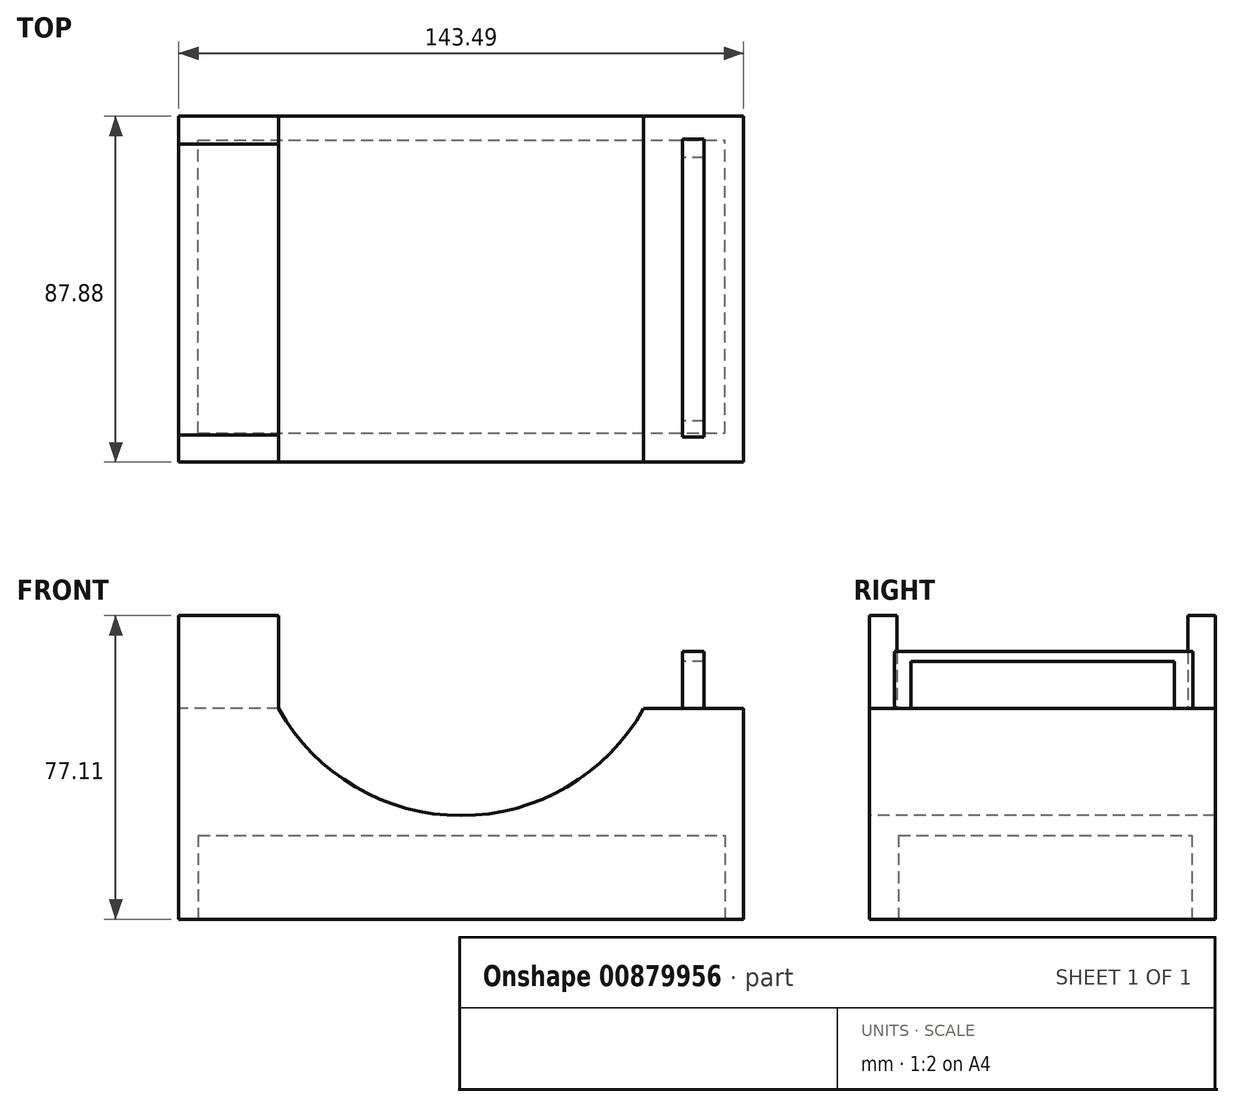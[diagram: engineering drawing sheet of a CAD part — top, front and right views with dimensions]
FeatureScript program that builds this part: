
annotation { "Feature Type Name" : "Feature", "Feature Type Description" : "" }
export const myFeature = defineFeature(function(context is Context, id is Id, definition is map)
    precondition{}
    {
        {
            var Q0;
            Q0=qCreatedBy(makeId("Front.planeOp"),FACE);
            var sketch = newSketch(context, id + "F0", { "sketchPlane" : qUnion([Q0])});
            skLineSegment(sketch, "E0.bottom", {"start": v(-31.97, 19.52) * mm, "end": v(60.72, 19.52) * mm});
            skLineSegment(sketch, "E0.top", {"start": v(-31.97, -33.97) * mm, "end": v(60.72, -33.97) * mm});
            skLineSegment(sketch, "E0.left", {"start": v(-31.97, 19.52) * mm, "end": v(-31.97, -33.97) * mm});
            skLineSegment(sketch, "E0.right", {"start": v(60.72, 19.52) * mm, "end": v(60.72, -33.97) * mm});
            skSolve(sketch);
        }
        {
            var Q0;
            Q0=makeQuery(id+"F0.imprint","IMPRINT",FACE,{"disambiguationData":[TD([[makeQuery(id+"F0.imprint","IMPRINT",EDGE,{"derivedFrom":sQuery(id+"F0.wireOp",EDGE,"E0.bottom")}),-1.0]])]});
            extrude(context, id + "F1", {"entities" : qUnion([Q0]), "depth" : 87.88 * mm, "offsetDistance" : 25.4 * mm});
        }
        {
            var Q0;
            Q0=makeQuery(id+"F1.opExtrude","CAP_FACE",FACE,{"disambiguationData":[OSD([sQuery(id+"F0.wireOp",EDGE,"E0.bottom"),sQuery(id+"F0.wireOp",EDGE,"E0.top"),sQuery(id+"F0.wireOp",EDGE,"E0.left"),sQuery(id+"F0.wireOp",EDGE,"E0.right")])],"isStart":false});
            var sketch = newSketch(context, id + "F2", { "sketchPlane" : qUnion([Q0])});
            skArc(sketch, "E1", {"start": v(-31.97, 19.52) * mm, "mid": v(14.38, -7.65) * mm, "end": v(60.72, 19.52) * mm});
            skSolve(sketch);
        }
        {
            var Q0;
            Q0=makeQuery(id+"F2.imprint","IMPRINT",FACE,{"disambiguationData":[TD([[makeQuery(id+"F2.imprint","IMPRINT",EDGE,{"derivedFrom":sQuery(id+"F2.wireOp",EDGE,"E1")}),1.0]])]});
            extrude(context, id + "F3", {"entities" : qUnion([Q0]), "operationType" : NewBodyOperationType.REMOVE, "oppositeDirection" : true, "depth" : 162.8 * mm, "offsetDistance" : 25.4 * mm});
        }
        {
            var Q0;
            Q0=makeQuery(id+"F1.opExtrude","SWEPT_FACE",FACE,{"disambiguationData":[OSD([sQuery(id+"F0.wireOp",EDGE,"E0.right")])]});
            extrude(context, id + "F4", {"entities" : qUnion([Q0]), "operationType" : NewBodyOperationType.ADD, "depth" : 25.4 * mm, "offsetDistance" : 25.4 * mm});
        }
        {
            var Q0;
            Q0=makeQuery(id+"F1.opExtrude","SWEPT_FACE",FACE,{"disambiguationData":[OSD([sQuery(id+"F0.wireOp",EDGE,"E0.left")])]});
            extrude(context, id + "F5", {"entities" : qUnion([Q0]), "operationType" : NewBodyOperationType.ADD, "depth" : 25.4 * mm, "offsetDistance" : 25.4 * mm});
        }
        {
            var Q0;
            Q0=makeQuery(id+"F4.opExtrude","SWEPT_FACE",FACE,{"disambiguationData":[OSD([sQuery(id+"F0.wireOp",EDGE,"E0.bottom"),sQuery(id+"F0.wireOp",EDGE,"E0.right"),sQuery(id+"F2.wireOp",EDGE,"E1")])]});
            var sketch = newSketch(context, id + "F6", { "sketchPlane" : qUnion([Q0])});
            skLineSegment(sketch, "E2.bottom", {"start": v(70.54, -81.5) * mm, "end": v(76.1, -81.5) * mm});
            skLineSegment(sketch, "E2.top", {"start": v(70.54, -5.79) * mm, "end": v(76.1, -5.79) * mm});
            skLineSegment(sketch, "E2.left", {"start": v(70.54, -81.5) * mm, "end": v(70.54, -5.79) * mm});
            skLineSegment(sketch, "E2.right", {"start": v(76.1, -81.5) * mm, "end": v(76.1, -5.79) * mm});
            skSolve(sketch);
        }
        {
            var Q0;
            Q0 = qSketchRegion(id + "F6", true);
            extrude(context, id + "F7", {"entities" : qUnion([Q0]), "operationType" : NewBodyOperationType.ADD, "depth" : 14.48 * mm, "offsetDistance" : 25.4 * mm});
        }
        {
            var Q0;
            Q0=makeQuery(id+"F7.opExtrude","SWEPT_FACE",FACE,{"disambiguationData":[OSD([sQuery(id+"F6.wireOp",EDGE,"E2.left")])]});
            var sketch = newSketch(context, id + "F8", { "sketchPlane" : qUnion([Q0])});
            skLineSegment(sketch, "E3.bottom", {"start": v(10.46, 19.52) * mm, "end": v(77.4, 19.52) * mm});
            skLineSegment(sketch, "E3.top", {"start": v(10.46, 31.47) * mm, "end": v(77.4, 31.47) * mm});
            skLineSegment(sketch, "E3.left", {"start": v(10.46, 19.52) * mm, "end": v(10.46, 31.47) * mm});
            skLineSegment(sketch, "E3.right", {"start": v(77.4, 19.52) * mm, "end": v(77.4, 31.47) * mm});
            skSolve(sketch);
        }
        {
            var Q0;
            Q0 = qSketchRegion(id + "F8", true);
            extrude(context, id + "F9", {"entities" : qUnion([Q0]), "operationType" : NewBodyOperationType.REMOVE, "oppositeDirection" : true, "depth" : 64.26 * mm, "offsetDistance" : 25.4 * mm});
        }
        {
            var Q0;
            {var subQ0=sQuery(id+"F0.wireOp",EDGE,"E0.top");Q0=makeQuery(id+"F5.boolean.opBoolean","MERGE",FACE,{"derivedFrom":[makeQuery(id+"F4.boolean.opBoolean","MERGE",FACE,{"derivedFrom":[makeQuery(id+"F1.opExtrude","SWEPT_FACE",FACE,{"disambiguationData":[OSD([subQ0])]}),makeQuery(id+"F4.opExtrude","SWEPT_FACE",FACE,{"disambiguationData":[OSD([subQ0,sQuery(id+"F0.wireOp",EDGE,"E0.right")])]})]}),makeQuery(id+"F5.opExtrude","SWEPT_FACE",FACE,{"disambiguationData":[OSD([subQ0,sQuery(id+"F0.wireOp",EDGE,"E0.left")])]})]});}
            var sketch = newSketch(context, id + "F10", { "sketchPlane" : qUnion([Q0])});
            skLineSegment(sketch, "E4.bottom", {"start": v(-52.46, 80.5) * mm, "end": v(81.45, 80.5) * mm});
            skLineSegment(sketch, "E4.top", {"start": v(-52.46, 6.03) * mm, "end": v(81.45, 6.03) * mm});
            skLineSegment(sketch, "E4.left", {"start": v(-52.46, 80.5) * mm, "end": v(-52.46, 6.03) * mm});
            skLineSegment(sketch, "E4.right", {"start": v(81.45, 80.5) * mm, "end": v(81.45, 6.03) * mm});
            skSolve(sketch);
        }
        {
            var Q0;
            Q0 = qSketchRegion(id + "F10", true);
            extrude(context, id + "F11", {"entities" : qUnion([Q0]), "operationType" : NewBodyOperationType.REMOVE, "oppositeDirection" : true, "depth" : 21.34 * mm, "offsetDistance" : 25.4 * mm});
        }
        {
            var Q0;
            Q0=makeQuery(id+"F5.opExtrude","SWEPT_FACE",FACE,{"disambiguationData":[OSD([sQuery(id+"F0.wireOp",EDGE,"E0.bottom"),sQuery(id+"F0.wireOp",EDGE,"E0.left"),sQuery(id+"F2.wireOp",EDGE,"E1")])]});
            extrude(context, id + "F12", {"entities" : qUnion([Q0]), "operationType" : NewBodyOperationType.ADD, "depth" : 25.4 * mm, "offsetDistance" : 25.4 * mm});
        }
        {
            var Q0;
            Q0=makeQuery(id+"F12.opExtrude","CAP_FACE",FACE,{"disambiguationData":[OSD([sQuery(id+"F0.wireOp",EDGE,"E0.bottom"),sQuery(id+"F0.wireOp",EDGE,"E0.left"),sQuery(id+"F2.wireOp",EDGE,"E1")])],"isStart":false});
            var sketch = newSketch(context, id + "F13", { "sketchPlane" : qUnion([Q0])});
            skSolve(sketch);
        }
        {
            var Q0;
            {var subQ1=sQuery(id+"F0.wireOp",EDGE,"E0.left");var subQ2=sQuery(id+"F0.wireOp",EDGE,"E0.bottom");Q0=makeQuery(id+"F13.imprint","IMPRINT",FACE,{"disambiguationData":[TD([[makeQuery(id+"F13.imprint","IMPRINT",EDGE,{"derivedFrom":makeQuery(id+"F12.opExtrude","CAP_EDGE",EDGE,{"disambiguationData":[OSD([subQ2,subQ1])],"isStart":false})}),-1.0]])]});}
            extrude(context, id + "F14", {"entities" : qUnion([Q0]), "operationType" : NewBodyOperationType.REMOVE, "oppositeDirection" : true, "depth" : 25.4 * mm, "offsetDistance" : 25.4 * mm});
        }
        {
            var Q0;
            Q0=makeQuery(id+"F14.boolean.opBoolean","COPY",FACE,{"derivedFrom":makeQuery(id+"F14.opExtrude","CAP_FACE",FACE,{"disambiguationData":[OSD([sQuery(id+"F0.wireOp",EDGE,"E0.bottom"),sQuery(id+"F0.wireOp",EDGE,"E0.left"),sQuery(id+"F2.wireOp",EDGE,"E1")])],"isStart":false})});
            var sketch = newSketch(context, id + "F15", { "sketchPlane" : qUnion([Q0])});
            skLineSegment(sketch, "E5.bottom", {"start": v(-31.97, -80.92) * mm, "end": v(-57.37, -80.92) * mm});
            skLineSegment(sketch, "E5.top", {"start": v(-31.97, -87.88) * mm, "end": v(-57.37, -87.88) * mm});
            skLineSegment(sketch, "E5.left", {"start": v(-31.97, -80.92) * mm, "end": v(-31.97, -87.88) * mm});
            skLineSegment(sketch, "E5.right", {"start": v(-57.37, -80.92) * mm, "end": v(-57.37, -87.88) * mm});
            skLineSegment(sketch, "E6.bottom", {"start": v(-31.97, 0) * mm, "end": v(-57.37, 0) * mm});
            skLineSegment(sketch, "E6.top", {"start": v(-31.97, -7.01) * mm, "end": v(-57.37, -7.01) * mm});
            skLineSegment(sketch, "E6.left", {"start": v(-31.97, 0) * mm, "end": v(-31.97, -7.01) * mm});
            skLineSegment(sketch, "E6.right", {"start": v(-57.37, 0) * mm, "end": v(-57.37, -7.01) * mm});
            skSolve(sketch);
        }
        {
            var Q0;
            Q0=makeQuery(id+"F15.imprint","IMPRINT",FACE,{"disambiguationData":[TD([[makeQuery(id+"F15.imprint","IMPRINT",EDGE,{"derivedFrom":sQuery(id+"F15.wireOp",EDGE,"E6.bottom")}),-1.0]])]});
            var Q1;
            Q1=makeQuery(id+"F15.imprint","IMPRINT",FACE,{"disambiguationData":[TD([[makeQuery(id+"F15.imprint","IMPRINT",EDGE,{"derivedFrom":sQuery(id+"F15.wireOp",EDGE,"E5.bottom")}),1.0]])]});
            extrude(context, id + "F16", {"entities" : qUnion([Q0, Q1]), "operationType" : NewBodyOperationType.ADD, "depth" : 42.42 * mm, "offsetDistance" : 25.4 * mm});
        }
        {
            var Q0;
            Q0=makeQuery(id+"F16.opExtrude","CAP_FACE",FACE,{"disambiguationData":[OSD([sQuery(id+"F15.wireOp",EDGE,"E5.bottom"),sQuery(id+"F15.wireOp",EDGE,"E5.top"),sQuery(id+"F15.wireOp",EDGE,"E5.left"),sQuery(id+"F15.wireOp",EDGE,"E5.right")])],"isStart":false});
            var Q1;
            Q1=makeQuery(id+"F16.opExtrude","CAP_FACE",FACE,{"disambiguationData":[OSD([sQuery(id+"F15.wireOp",EDGE,"E6.bottom"),sQuery(id+"F15.wireOp",EDGE,"E6.top"),sQuery(id+"F15.wireOp",EDGE,"E6.left"),sQuery(id+"F15.wireOp",EDGE,"E6.right")])],"isStart":false});
            extrude(context, id + "F17", {"entities" : qUnion([Q0, Q1]), "operationType" : NewBodyOperationType.REMOVE, "oppositeDirection" : true, "depth" : 18.8 * mm, "offsetDistance" : 25.4 * mm});
        }
    });
